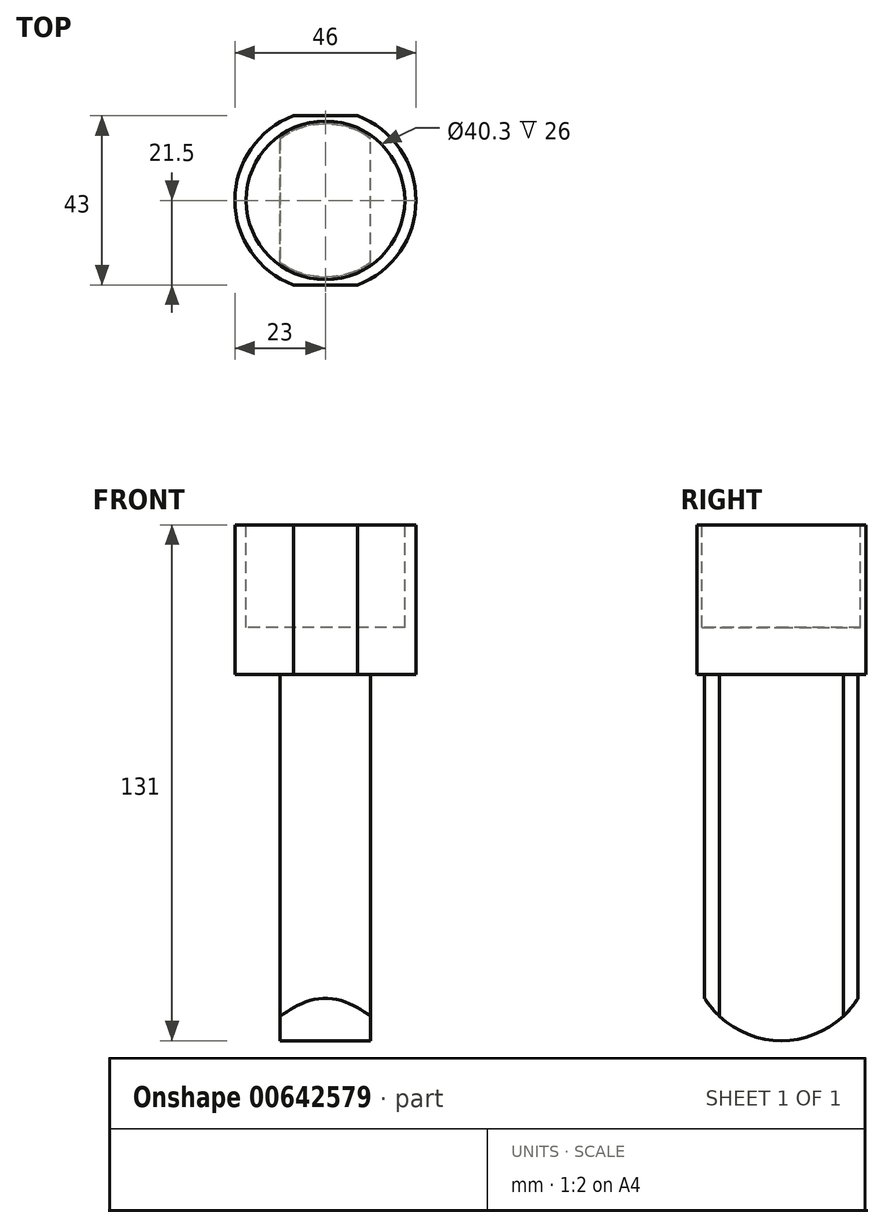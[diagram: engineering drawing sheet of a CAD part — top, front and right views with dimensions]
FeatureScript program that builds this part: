
annotation { "Feature Type Name" : "Feature", "Feature Type Description" : "" }
export const myFeature = defineFeature(function(context is Context, id is Id, definition is map)
    precondition{}
    {
        {
            var Q0;
            Q0=qCreatedBy(makeId("Top.planeOp"),FACE);
            var sketch = newSketch(context, id + "F0", { "sketchPlane" : qUnion([Q0])});
            skArc(sketch, "E0", {"start": v(-8.17, 21.5) * mm, "mid": v(-23, 0) * mm, "end": v(-8.17, -21.5) * mm});
            skLineSegment(sketch, "E1", {"start": v(-8.17, 21.5) * mm, "end": v(8.17, 21.5) * mm});
            skLineSegment(sketch, "E2.MirrorCS", {"start": v(-8.17, -21.5) * mm, "end": v(8.17, -21.5) * mm});
            skArc(sketch, "E3.trimOffspring", {"start": v(8.17, -21.5) * mm, "mid": v(23, 0) * mm, "end": v(8.17, 21.5) * mm});
            skSolve(sketch);
        }
        {
            var Q0;
            Q0=makeQuery(id+"F0.imprint","IMPRINT",FACE,{"disambiguationData":[TD([[makeQuery(id+"F0.imprint","IMPRINT",EDGE,{"derivedFrom":sQuery(id+"F0.wireOp",EDGE,"E0")}),1.0]])]});
            extrude(context, id + "F1", {"entities" : qUnion([Q0]), "depth" : 38 * mm, "offsetDistance" : 25 * mm});
        }
        {
            var Q0;
            Q0=makeQuery(id+"F1.opExtrude","CAP_FACE",FACE,{"disambiguationData":[OSD([sQuery(id+"F0.wireOp",EDGE,"E0"),sQuery(id+"F0.wireOp",EDGE,"E1"),sQuery(id+"F0.wireOp",EDGE,"E2.MirrorCS"),sQuery(id+"F0.wireOp",EDGE,"E3.trimOffspring")])],"isStart":false});
            var sketch = newSketch(context, id + "F2", { "sketchPlane" : qUnion([Q0])});
            skCircle(sketch, "E4", {"center": v(0, 0) * mm, "radius": 20.15 * mm});
            skSolve(sketch);
        }
        {
            var Q0;
            Q0=makeQuery(id+"F2.imprint","IMPRINT",FACE,{"disambiguationData":[TD([[makeQuery(id+"F2.imprint","IMPRINT",EDGE,{"derivedFrom":sQuery(id+"F2.wireOp",EDGE,"E4")}),1.0]])]});
            extrude(context, id + "F3", {"entities" : qUnion([Q0]), "operationType" : NewBodyOperationType.REMOVE, "oppositeDirection" : true, "depth" : 26 * mm, "offsetDistance" : 25 * mm});
        }
        {
            var Q0;
            Q0=makeQuery(id+"F1.opExtrude","CAP_FACE",FACE,{"disambiguationData":[OSD([sQuery(id+"F0.wireOp",EDGE,"E0"),sQuery(id+"F0.wireOp",EDGE,"E1"),sQuery(id+"F0.wireOp",EDGE,"E2.MirrorCS"),sQuery(id+"F0.wireOp",EDGE,"E3.trimOffspring")])],"isStart":true});
            var sketch = newSketch(context, id + "F4", { "sketchPlane" : qUnion([Q0])});
            skArc(sketch, "E5", {"start": v(11.5, 15.75) * mm, "mid": v(0, 19.5) * mm, "end": v(-11.5, 15.75) * mm});
            skLineSegment(sketch, "E6", {"start": v(-11.5, 15.75) * mm, "end": v(-11.5, -15.75) * mm});
            skLineSegment(sketch, "E7.MirrorCS", {"start": v(11.5, 15.75) * mm, "end": v(11.5, -15.75) * mm});
            skArc(sketch, "E8.trimOffspring", {"start": v(-11.5, -15.75) * mm, "mid": v(0, -19.5) * mm, "end": v(11.5, -15.75) * mm});
            skSolve(sketch);
        }
        {
            var Q0;
            Q0=makeQuery(id+"F4.imprint","IMPRINT",FACE,{"disambiguationData":[TD([[makeQuery(id+"F4.imprint","IMPRINT",EDGE,{"derivedFrom":sQuery(id+"F4.wireOp",EDGE,"E5")}),1.0]])]});
            extrude(context, id + "F5", {"entities" : qUnion([Q0]), "operationType" : NewBodyOperationType.ADD, "depth" : 93 * mm, "offsetDistance" : 25 * mm});
        }
        {
            var Q0;
            Q0=makeQuery(id+"F5.opExtrude","SWEPT_FACE",FACE,{"disambiguationData":[OSD([sQuery(id+"F4.wireOp",EDGE,"E6")])]});
            var sketch = newSketch(context, id + "F6", { "sketchPlane" : qUnion([Q0])});
            skArc(sketch, "E9", {"start": v(-21.55, -78.03) * mm, "mid": v(-0.06, -93) * mm, "end": v(21.5, -78.15) * mm});
            skLineSegment(sketch, "E10", {"start": v(-21.55, -78.03) * mm, "end": v(-24.34, -100.79) * mm});
            skLineSegment(sketch, "E11", {"start": v(-24.34, -100.79) * mm, "end": v(39.53, -103.87) * mm});
            skLineSegment(sketch, "E12", {"start": v(39.53, -103.87) * mm, "end": v(21.5, -78.15) * mm});
            skSolve(sketch);
        }
        {
            var Q0;
            {var subQ0=sQuery(id+"F6.wireOp",EDGE,"E10");Q0=makeQuery(id+"F6.imprint","IMPRINT",FACE,{"disambiguationData":[TD([[makeQuery(id+"F6.imprint","IMPRINT",EDGE,{"derivedFrom":subQ0}),1.0]])]});}
            var Q1;
            {var subQ0=sQuery(id+"F6.wireOp",EDGE,"E9");var subQ1=sQuery(id+"F4.wireOp",EDGE,"E6");var subQ4=makeQuery(id+"F5.opExtrude","CAP_EDGE",EDGE,{"disambiguationData":[OSD([subQ1])],"isStart":false});var subQ5=makeQuery(id+"F6.imprint","INTERSECT",VERTEX,{"derivedFrom":[subQ4,subQ0]});Q1=makeQuery(id+"F6.imprint","IMPRINT",FACE,{"disambiguationData":[TD([[makeQuery(id+"F6.imprint","IMPRINT",EDGE,{"disambiguationData":[TD([[subQ5,-1.0]])],"derivedFrom":subQ0}),-1.0]])]});}
            var Q2;
            {var subQ0=sQuery(id+"F6.wireOp",EDGE,"E9");var subQ1=sQuery(id+"F4.wireOp",EDGE,"E6");var subQ4=makeQuery(id+"F5.opExtrude","CAP_EDGE",EDGE,{"disambiguationData":[OSD([subQ1])],"isStart":false});var subQ5=makeQuery(id+"F6.imprint","INTERSECT",VERTEX,{"derivedFrom":[subQ4,subQ0]});Q2=makeQuery(id+"F6.imprint","IMPRINT",FACE,{"disambiguationData":[TD([[makeQuery(id+"F6.imprint","IMPRINT",EDGE,{"disambiguationData":[TD([[subQ5,1.0]])],"derivedFrom":subQ0}),-1.0]])]});}
            extrude(context, id + "F7", {"entities" : qUnion([Q0, Q1, Q2]), "operationType" : NewBodyOperationType.REMOVE, "endBound" : BoundingType.THROUGH_ALL, "oppositeDirection" : true, "depth" : 25 * mm, "offsetDistance" : 25 * mm});
        }
    });
